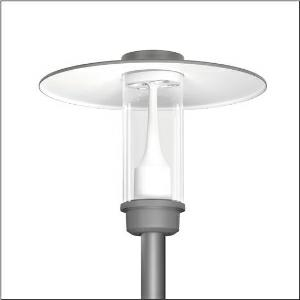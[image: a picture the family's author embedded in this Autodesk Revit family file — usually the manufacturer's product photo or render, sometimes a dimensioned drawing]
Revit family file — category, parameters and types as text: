
# Revit family: litepole_2_iq___pl1_2s_5xa5425jf14h000022_13c4
name_source: partatom
category: Lighting Fixtures
units: mm (PartAtom-declared; Revit-internal decimal feet)

## family parameters
Cut with Voids When Loaded = No
Host = Face
Light Source = No
Part Type = Normal
Room Calculation Point = No
Round Connector Dimension = Use Diameter
Shared = No

## types (1)
- --- (1 x LED, 2990 lm, 19.3 W, 3000K)
    Apparent Load = 19 VA
    CIE Flux Codes = 22 60 92 98 100
    Color Rendering = 70
    Color Temperature = 3000K
    Default Elevation = 1800 mm
    Description = Litepole 2 iQ, mast luminaire, Module 540 iQ-SR, primary light control with 3 zone facetted reflector, of plastic, silver coated, highly specular, structured, primary optical cover: cover, of PMMA, transparent, light distribution: PL1.2s, light emission: direct distribution, primary light characteristic: symmetric, installation type: post-top, LED, High Power LED, rated luminous flux: 2.990lm, luminous efficacy: 155lm/W, light colour: 730, colour temperature: 3000K, control gear: iQ Street-Remote, control: Street-Remote, Auto-Match, Temp-Guard, Lumen-Switch, Night-Set, Smart-Wire, Light-Fading, Desk-Remote (wireless, voltage-free reading and setting of iQ features in the workshop via application-optimized NFC function/RFID function), optimised constant luminous flux control (CLO 2.0), pre-setting: logarithmic dimming characteristic, mains connection: 230..240V, AC, 50/60Hz, connection cable pre-assembled, cable length: 5,5m, wiring characteristics: H07RN-F, start of lifetime: 19W, end of service life: 21W, reduction: 10W, luminaire housing, upper part, of aluminium, coated, SITECO metallic grey (DB 702S), diameter: 750mm, height: 590mm, spigot size: d x l = 76 x 70mm (post-top) | with reducer (optional accessory) 60 x 70mm, mounting height: 3..5m, post-top mast mounting element, of diecast aluminium, coated, SITECO metallic grey (DB 702S), Module 540 iQ-SR, traffic white (RAL 9016), equipment: standard, protection rating (complete): IP65, insulation class (complete): insulation class II (safety insulation), certification: CE, ENEC, VDE, packaging unit: 1 piece

Light Distribution: PL1.2s
    Height = 590 mm
    Lamp = 1 x LED
    Lamp Light Flux = 2990 lm
    Lamp Power = 19.3 W
    Lamp count = 1
    Length = 750 mm
    Luminous efficacy = 155 lm/W
    Manufacturer = Siteco
    ModVariant = No
    Model = 5XA5425JF14H000022
    Number of Poles = 1
    OnlyDefault = Yes
    Power Factor = 1
    Product Name = Litepole 2 iQ | PL1.2s
    Product group = mast luminaire | pylon top
    ProductGroupID = 6100
    Protection Class = Protection class II
    Protection Degree = IP 65
    RLX_Detail_Level = 1
    RLX_Emergency_Light_Flux = 0 lm
    RLX_Emergency_Type = 0
    RLX_Emergency_Type_DB = No
    RlxData = <blob elided: 29413 chars, md5=c0a979b6>
    Socket = socket
    Standby Power = 0 W
    System Light Flux = 2990 lm
    System Power = 19 W
    Type Comments = factory setting: luminous flux: 100 % | dim-lin: 254 | 403 mA
    Type Image = l_1006518.jpg
    URL = http://relux.com
    VarID = @adj_144069
    Voltage = 0 V
    Weight = 0.00 kg
    Width = 0 mm  [stored 0 ft]

note: [stored X ft] marks values corroborated as IEEE doubles in the binary element streams (Revit-internal decimal feet)

## geometry (parser evidence)
native form markers: Blend x4, Sweep x10
no freeform markers — native parametric forms only
